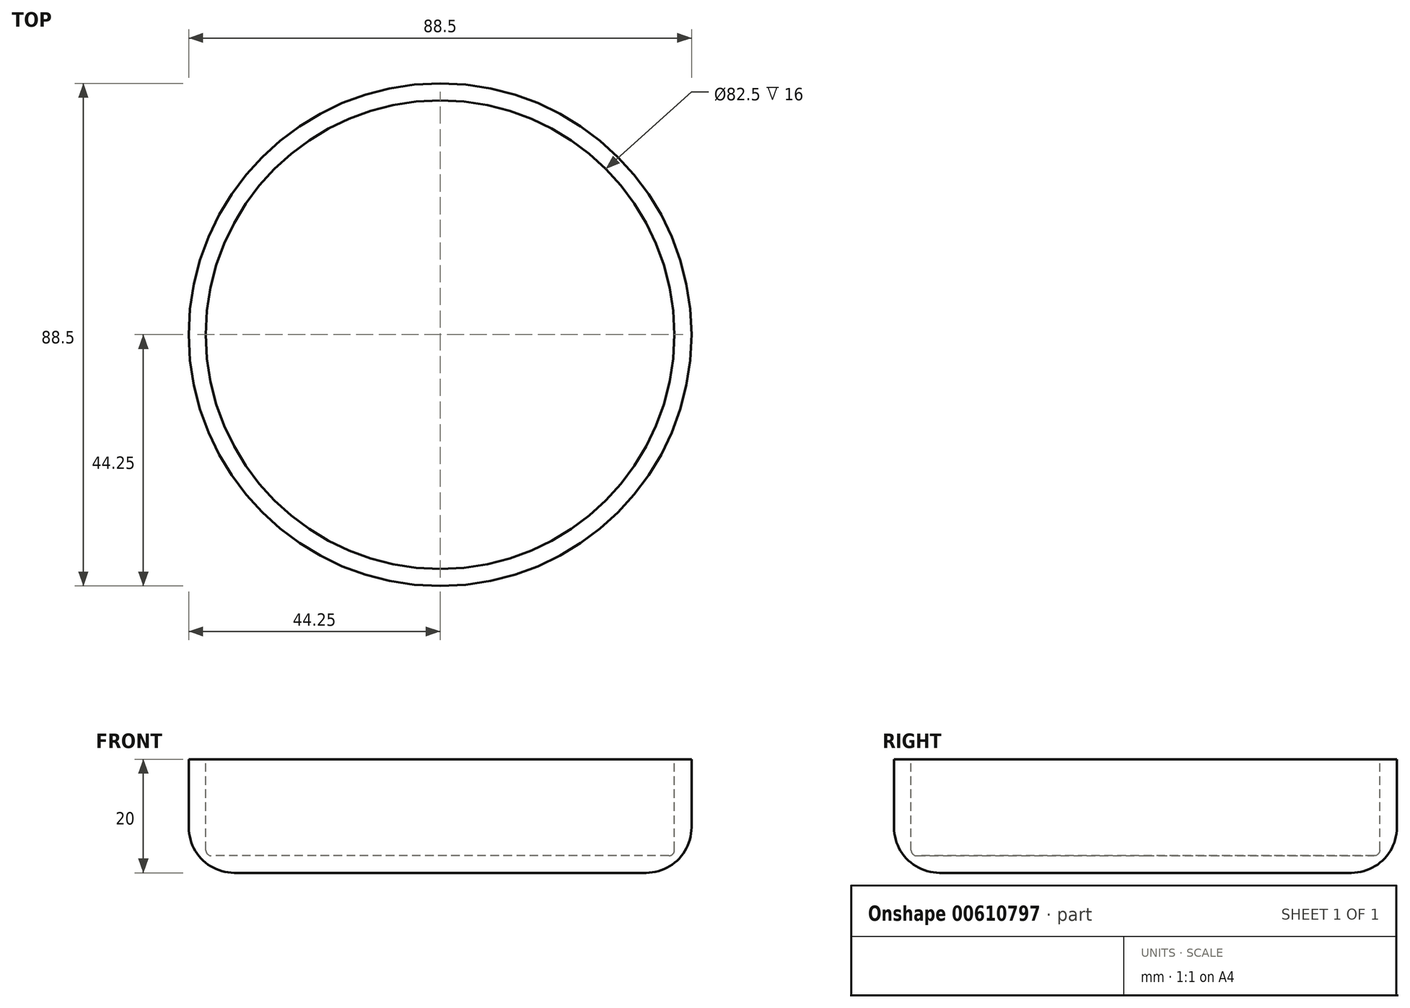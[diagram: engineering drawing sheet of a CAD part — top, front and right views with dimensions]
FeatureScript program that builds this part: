
annotation { "Feature Type Name" : "Feature", "Feature Type Description" : "" }
export const myFeature = defineFeature(function(context is Context, id is Id, definition is map)
    precondition{}
    {
        {
            var Q0;
            Q0=qCreatedBy(makeId("Top.planeOp"),FACE);
            var sketch = newSketch(context, id + "F0", { "sketchPlane" : qUnion([Q0])});
            skCircle(sketch, "E0", {"center": v(0, 0) * mm, "radius": 44.25 * mm});
            skSolve(sketch);
        }
        {
            var Q0;
            Q0=makeQuery(id+"F0.imprint","IMPRINT",FACE,{"disambiguationData":[TD([[makeQuery(id+"F0.imprint","IMPRINT",EDGE,{"derivedFrom":sQuery(id+"F0.wireOp",EDGE,"E0")}),1.0]])]});
            extrude(context, id + "F1", {"entities" : qUnion([Q0]), "depth" : 20 * mm, "offsetDistance" : 25 * mm});
        }
        {
            var Q0;
            Q0=makeQuery(id+"F1.opExtrude","CAP_FACE",FACE,{"disambiguationData":[OSD([sQuery(id+"F0.wireOp",EDGE,"E0")])],"isStart":false});
            var sketch = newSketch(context, id + "F2", { "sketchPlane" : qUnion([Q0])});
            skCircle(sketch, "E1", {"center": v(0, 0) * mm, "radius": 41.25 * mm});
            skSolve(sketch);
        }
        {
            var Q0;
            Q0=makeQuery(id+"F2.imprint","IMPRINT",FACE,{"disambiguationData":[TD([[makeQuery(id+"F2.imprint","IMPRINT",EDGE,{"derivedFrom":sQuery(id+"F2.wireOp",EDGE,"E1")}),1.0]])]});
            extrude(context, id + "F3", {"entities" : qUnion([Q0]), "operationType" : NewBodyOperationType.REMOVE, "oppositeDirection" : true, "depth" : 17 * mm, "offsetDistance" : 25 * mm});
        }
        {
            var Q0;
            Q0=makeQuery(id+"F3.boolean.opBoolean","COPY",EDGE,{"derivedFrom":makeQuery(id+"F3.opExtrude","CAP_EDGE",EDGE,{"disambiguationData":[OSD([sQuery(id+"F2.wireOp",EDGE,"E1")])],"isStart":false})});
            fillet(context, id + "F4", {"entities" : qUnion([Q0]), "radius" : 1 * mm, "tangentPropagation" : true, "allowEdgeOverflow" : false});
        }
        {
            var Q0;
            Q0=makeQuery(id+"F1.opExtrude","CAP_EDGE",EDGE,{"disambiguationData":[OSD([sQuery(id+"F0.wireOp",EDGE,"E0")])],"isStart":true});
            fillet(context, id + "F5", {"entities" : qUnion([Q0]), "radius" : 8 * mm, "tangentPropagation" : true, "allowEdgeOverflow" : false});
        }
    });
